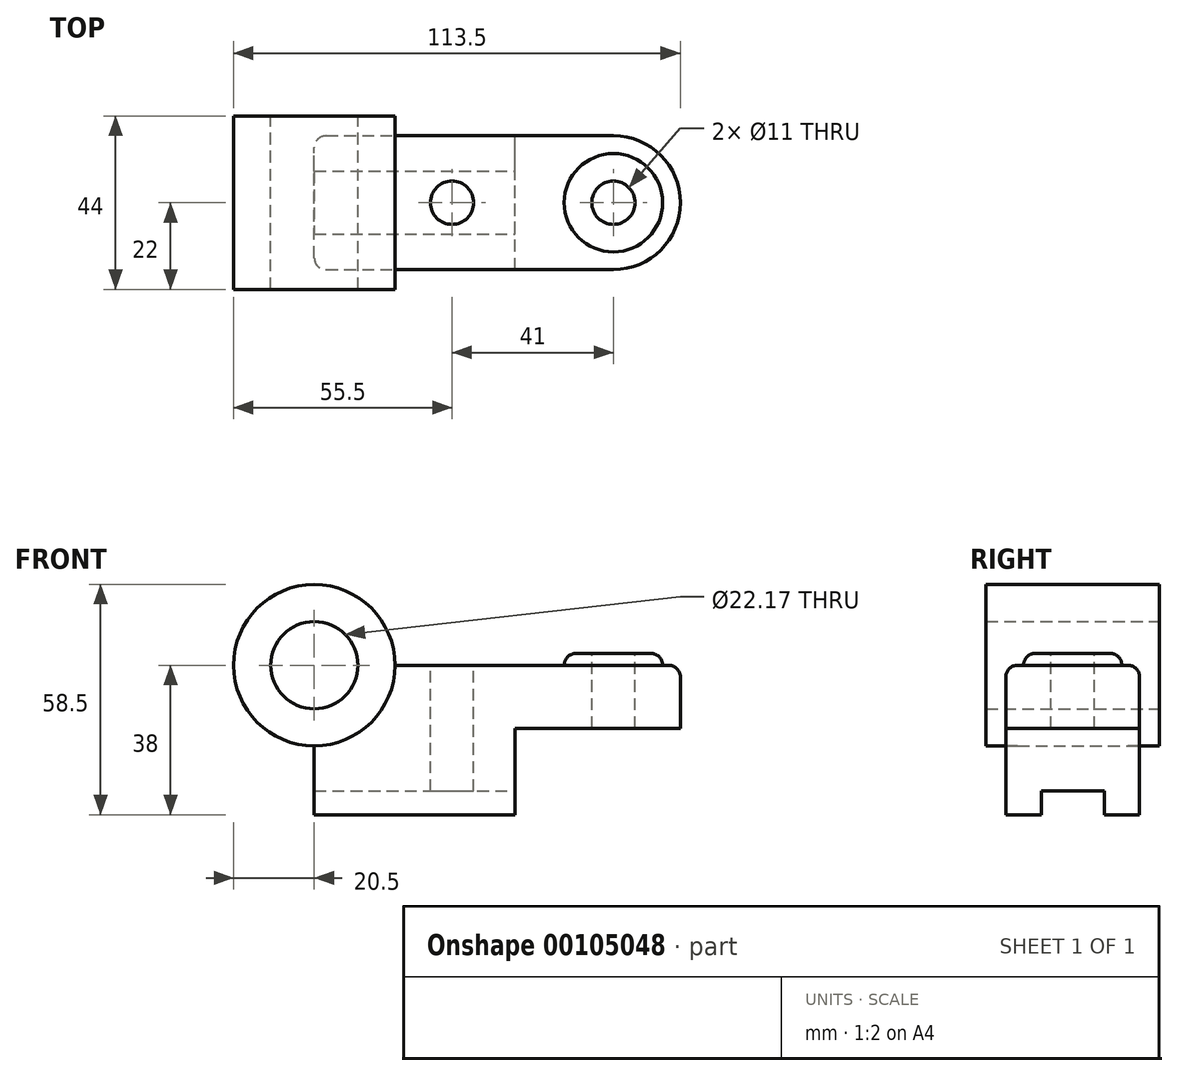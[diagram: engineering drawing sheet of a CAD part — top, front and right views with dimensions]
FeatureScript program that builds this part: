
annotation { "Feature Type Name" : "Feature", "Feature Type Description" : "" }
export const myFeature = defineFeature(function(context is Context, id is Id, definition is map)
    precondition{}
    {
        {
            var Q0;
            Q0=qCreatedBy(makeId("Front.planeOp"),FACE);
            var sketch = newSketch(context, id + "F0", { "sketchPlane" : qUnion([Q0])});
            skLineSegment(sketch, "E0.bottom", {"start": v(0, 0) * mm, "end": v(51, 0) * mm});
            skLineSegment(sketch, "E0.top", {"start": v(0, 38) * mm, "end": v(76, 38) * mm});
            skLineSegment(sketch, "E0.left", {"start": v(0, 0) * mm, "end": v(0, 38) * mm});
            skLineSegment(sketch, "E0.right", {"start": v(76, 22) * mm, "end": v(76, 38) * mm});
            skLineSegment(sketch, "E1.top", {"start": v(76, 22) * mm, "end": v(51, 22) * mm});
            skLineSegment(sketch, "E1.right", {"start": v(51, 0) * mm, "end": v(51, 22) * mm});
            skCircle(sketch, "E2", {"center": v(0, 38) * mm, "radius": 11.09 * mm});
            skCircle(sketch, "E3", {"center": v(0, 38) * mm, "radius": 20.5 * mm});
            skSolve(sketch);
        }
        {
            var Q0;
            {var subQ2=sQuery(id+"F0.wireOp",EDGE,"E0.bottom");Q0=makeQuery(id+"F0.imprint","IMPRINT",FACE,{"disambiguationData":[TD([[makeQuery(id+"F0.imprint","IMPRINT",EDGE,{"derivedFrom":subQ2}),1.0]])]});}
            extrude(context, id + "F1", {"entities" : qUnion([Q0]), "endBound" : BoundingType.SYMMETRIC, "depth" : (17 * 2) * mm});
        }
        {
            var Q0;
            {var subQ0=sQuery(id+"F0.wireOp",EDGE,"E3");var subQ1=sQuery(id+"F0.wireOp",EDGE,"E0.top");var subQ2=makeQuery(id+"F0.imprint","INTERSECT",VERTEX,{"derivedFrom":[subQ1,subQ0]});Q0=makeQuery(id+"F0.imprint","IMPRINT",FACE,{"disambiguationData":[TD([[makeQuery(id+"F0.imprint","IMPRINT",EDGE,{"disambiguationData":[TD([[subQ2,1.0]])],"derivedFrom":subQ1}),1.0]])]});}
            var Q1;
            {var subQ0=sQuery(id+"F0.wireOp",EDGE,"E3");var subQ1=sQuery(id+"F0.wireOp",EDGE,"E0.top");var subQ2=makeQuery(id+"F0.imprint","INTERSECT",VERTEX,{"derivedFrom":[subQ1,subQ0]});Q1=makeQuery(id+"F0.imprint","IMPRINT",FACE,{"disambiguationData":[TD([[makeQuery(id+"F0.imprint","IMPRINT",EDGE,{"disambiguationData":[TD([[subQ2,1.0]])],"derivedFrom":subQ1}),-1.0]])]});}
            extrude(context, id + "F2", {"entities" : qUnion([Q0, Q1]), "operationType" : NewBodyOperationType.ADD, "endBound" : BoundingType.SYMMETRIC, "depth" : 44 * mm});
        }
        {
            var Q0;
            Q0=makeQuery(id+"F1.opExtrude","SWEPT_FACE",FACE,{"disambiguationData":[OSD([sQuery(id+"F0.wireOp",EDGE,"E0.top")])]});
            var sketch = newSketch(context, id + "F3", { "sketchPlane" : qUnion([Q0])});
            skArc(sketch, "E4", {"start": v(76, -17) * mm, "mid": v(93, 0) * mm, "end": v(76, 17) * mm});
            skSolve(sketch);
        }
        {
            var Q0;
            Q0=makeQuery(id+"F3.imprint","IMPRINT",FACE,{"disambiguationData":[TD([[makeQuery(id+"F3.imprint","IMPRINT",EDGE,{"derivedFrom":sQuery(id+"F3.wireOp",EDGE,"E4")}),1.0]])]});
            var Q1;
            Q1=makeQuery(id+"F1.opExtrude","SWEPT_FACE",FACE,{"disambiguationData":[OSD([sQuery(id+"F0.wireOp",EDGE,"E1.top")])]});
            extrude(context, id + "F4", {"entities" : qUnion([Q0]), "operationType" : NewBodyOperationType.ADD, "endBound" : BoundingType.UP_TO_SURFACE, "oppositeDirection" : true, "endBoundEntityFace" : qUnion([Q1]), "depth" : 25 * mm});
        }
        {
            var Q0;
            {var subQ0=sQuery(id+"F0.wireOp",EDGE,"E0.top");Q0=makeQuery(id+"F4.boolean.opBoolean","MERGE",FACE,{"derivedFrom":[makeQuery(id+"F1.opExtrude","SWEPT_FACE",FACE,{"disambiguationData":[OSD([subQ0])]}),makeQuery(id+"F4.opExtrude","CAP_FACE",FACE,{"disambiguationData":[OSD([subQ0,sQuery(id+"F0.wireOp",EDGE,"E0.right"),sQuery(id+"F3.wireOp",EDGE,"E4")])],"isStart":true})]});}
            var sketch = newSketch(context, id + "F5", { "sketchPlane" : qUnion([Q0])});
            skCircle(sketch, "E5", {"center": v(76, 0) * mm, "radius": 12.5 * mm});
            skSolve(sketch);
        }
        {
            var Q0;
            Q0=makeQuery(id+"F5.imprint","IMPRINT",FACE,{"disambiguationData":[TD([[makeQuery(id+"F5.imprint","IMPRINT",EDGE,{"derivedFrom":sQuery(id+"F5.wireOp",EDGE,"E5")}),1.0]])]});
            extrude(context, id + "F6", {"entities" : qUnion([Q0]), "operationType" : NewBodyOperationType.ADD, "depth" : 3 * mm});
        }
        {
            var Q0;
            Q0=makeQuery(id+"F6.opExtrude","CAP_FACE",FACE,{"disambiguationData":[OSD([sQuery(id+"F5.wireOp",EDGE,"E5")])],"isStart":false});
            var sketch = newSketch(context, id + "F7", { "sketchPlane" : qUnion([Q0])});
            skCircle(sketch, "E6", {"center": v(76, 0) * mm, "radius": 5.5 * mm});
            skCircle(sketch, "E7", {"center": v(35, 0) * mm, "radius": 5.5 * mm});
            skSolve(sketch);
        }
        {
            var Q0;
            Q0 = qSketchRegion(id + "F7", true);
            extrude(context, id + "F8", {"entities" : qUnion([Q0]), "operationType" : NewBodyOperationType.REMOVE, "endBound" : BoundingType.THROUGH_ALL, "oppositeDirection" : true, "depth" : 25 * mm});
        }
        {
            var Q0;
            Q0=makeQuery(id+"F1.opExtrude","SWEPT_FACE",FACE,{"disambiguationData":[OSD([sQuery(id+"F0.wireOp",EDGE,"E1.right")])]});
            var sketch = newSketch(context, id + "F9", { "sketchPlane" : qUnion([Q0])});
            skLineSegment(sketch, "E8.bottom", {"start": v(-8, 0) * mm, "end": v(8, 0) * mm});
            skLineSegment(sketch, "E8.top", {"start": v(-8, 6) * mm, "end": v(8, 6) * mm});
            skLineSegment(sketch, "E8.left", {"start": v(-8, 0) * mm, "end": v(-8, 6) * mm});
            skLineSegment(sketch, "E8.right", {"start": v(8, 0) * mm, "end": v(8, 6) * mm});
            skSolve(sketch);
        }
        {
            var Q0;
            Q0 = qSketchRegion(id + "F9", true);
            extrude(context, id + "F10", {"entities" : qUnion([Q0]), "operationType" : NewBodyOperationType.REMOVE, "endBound" : BoundingType.THROUGH_ALL, "oppositeDirection" : true, "depth" : 25 * mm});
        }
        {
            var Q0;
            Q0=makeQuery(id+"F6.opExtrude","CAP_EDGE",EDGE,{"disambiguationData":[OSD([sQuery(id+"F5.wireOp",EDGE,"E5")])],"isStart":false});
            var Q1;
            Q1=makeQuery(id+"F1.opExtrude","CAP_EDGE",EDGE,{"disambiguationData":[OSD([sQuery(id+"F0.wireOp",EDGE,"E3")])],"isStart":false});
            var Q2;
            Q2=makeQuery(id+"F1.opExtrude","SWEPT_EDGE",EDGE,{"disambiguationData":[OSD([sQuery(id+"F0.wireOp",EDGE,"E0.top"),sQuery(id+"F0.wireOp",EDGE,"E3")])]});
            var Q3;
            Q3=makeQuery(id+"F1.opExtrude","CAP_EDGE",EDGE,{"disambiguationData":[OSD([sQuery(id+"F0.wireOp",EDGE,"E3")])],"isStart":true});
            var Q4;
            Q4=makeQuery(id+"F1.opExtrude","SWEPT_EDGE",EDGE,{"disambiguationData":[OSD([sQuery(id+"F0.wireOp",EDGE,"E0.left"),sQuery(id+"F0.wireOp",EDGE,"E3")])]});
            var Q5;
            Q5=makeQuery(id+"F1.opExtrude","CAP_EDGE",EDGE,{"disambiguationData":[OSD([sQuery(id+"F0.wireOp",EDGE,"E0.left")])],"isStart":true});
            var Q6;
            Q6=makeQuery(id+"F1.opExtrude","CAP_EDGE",EDGE,{"disambiguationData":[OSD([sQuery(id+"F0.wireOp",EDGE,"E0.left")])],"isStart":false});
            fillet(context, id + "F11", {"entities" : qUnion([Q0, Q1, Q2, Q3, Q4, Q5, Q6]), "radius" : 3 * mm, "tangentPropagation" : true, "allowEdgeOverflow" : false});
        }
        {
            var Q0;
            Q0=makeQuery(id+"F1.opExtrude","CAP_EDGE",EDGE,{"disambiguationData":[OSD([sQuery(id+"F0.wireOp",EDGE,"E0.top")])],"isStart":false});
            fillet(context, id + "F12", {"entities" : qUnion([Q0]), "radius" : 3 * mm, "tangentPropagation" : true, "allowEdgeOverflow" : false});
        }
    });
